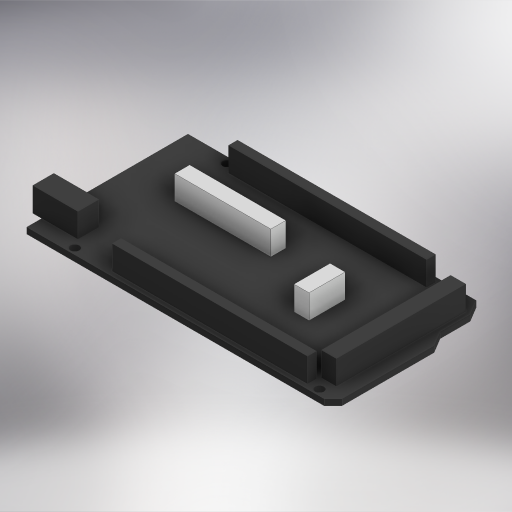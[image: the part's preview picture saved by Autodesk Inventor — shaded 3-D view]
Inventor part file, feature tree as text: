
AUTODESK INVENTOR PART (.ipt)
format: ipt  version: 2024 (Build 280153000, 153)  size: 420,864 bytes
history: native  units: mm
features: other x10, extrude x5, sketch x5
ambient origin geometry x8: Origin, YZ Plane, XZ Plane, XY Plane, X Axis, Y Axis, Z Axis, Center Point
bodies: Body1 (feature_tree)
feature tree (20):
  other  "Sólido1"
  extrude  "Extrusión1"  Depth=101.86mm
  extrude  "Extrusión7"  Depth=5.0mm
  extrude  "Extrusión6"  Depth=5.0mm
  extrude  "Extrusión4"  Depth=32.0mm
  extrude  "Extrusión8"  Depth=5.0mm
  sketch  "Boceto1"  dims[d0=53.61mm d1=101.86mm]
  sketch  "Boceto4"  dims[d2=2.0mm d3=0.0mm d19=5.0mm]
  sketch  "Boceto5"  dims[d20=12.0mm d21=5.0mm]
  sketch  "Boceto6"  dims[d22=32.0mm d23=20.0mm]
  sketch  "Boceto7"  dims[d24=8.0mm d25=0.0mm d33=5.0mm d34=7.0mm d35=3.0mm d36=15.0mm d37=8.0mm d38=0.0mm d39=3.0mm d40=3.0mm d41=3.0mm d42=6.5mm d43=2.0mm d44=6.0mm d45=10.0mm d46=3.0mm d47=10.0mm d48=10.0mm d49=3.0mm d50=2.0mm d51=15.0mm d52=3.0mm d53=2.0mm d54=14.0mm d55=3.0mm d56=2.0mm d57=15.0mm d58=3.0mm d59=0.0mm d60=1.5mm d61=5.0mm d62=5.0mm d63=43.0mm d64=1.5mm d65=3.0mm d66=10.0mm d67=65.0mm d68=1.5mm d69=3.0mm d70=15.0mm d71=18.0mm d72=8.0mm d73=0.0mm d17=0.5mm d18=0.872665mm d31=0.5mm d32=0.872665mm]
  other  "Finish1"
  other  "Finish2"
  other  "Finish3"
  other  "Finish4"
  other  "Finish5"
  other  "Finish6"
  other  "Finish7"
  other  "Finish8"
  other  "Finish9"
